# Revit family: Haworth_ActiveComponents_Screen_Corner
name_source: partatom
category: Furniture Systems
revit_build: Autodesk Revit 2018 (Build: 20170223_1515(x64)
units: mm (PartAtom-declared; Revit-internal decimal feet)

## family parameters
Always vertical = Yes
Cut with Voids When Loaded = No
OmniClass Number = 23.40.70.14.64.21
OmniClass Title = Systems Furniture
Part Type = Normal
Room Calculation Point = No
Round Connector Dimension = Use Diameter
Shared = No
Work Plane-Based = No

## types (1)
- 45w 24h
    Actual Depth = 29/32"
    Actual Height = 24"
    Actual Width = 44 1/8"
    Assembly Code = E2020200
    Description = Haworth Active Components Screen Corner - 45w 24h
    Frame Height = 26 3/4"
    Manufacturer = Haworth
    Model = Haworth Active Components Screen Corner - 45w 24h
    Revision Number = 1
    Size = Verify Final Dim. w/ Haworth
    URL = https://www.haworth.com
    URL - Product = http://www.haworth.com
    Warranty = http://www.haworth.com

## geometry (parser evidence)
native form markers: Sweep x3
no freeform markers — native parametric forms only
